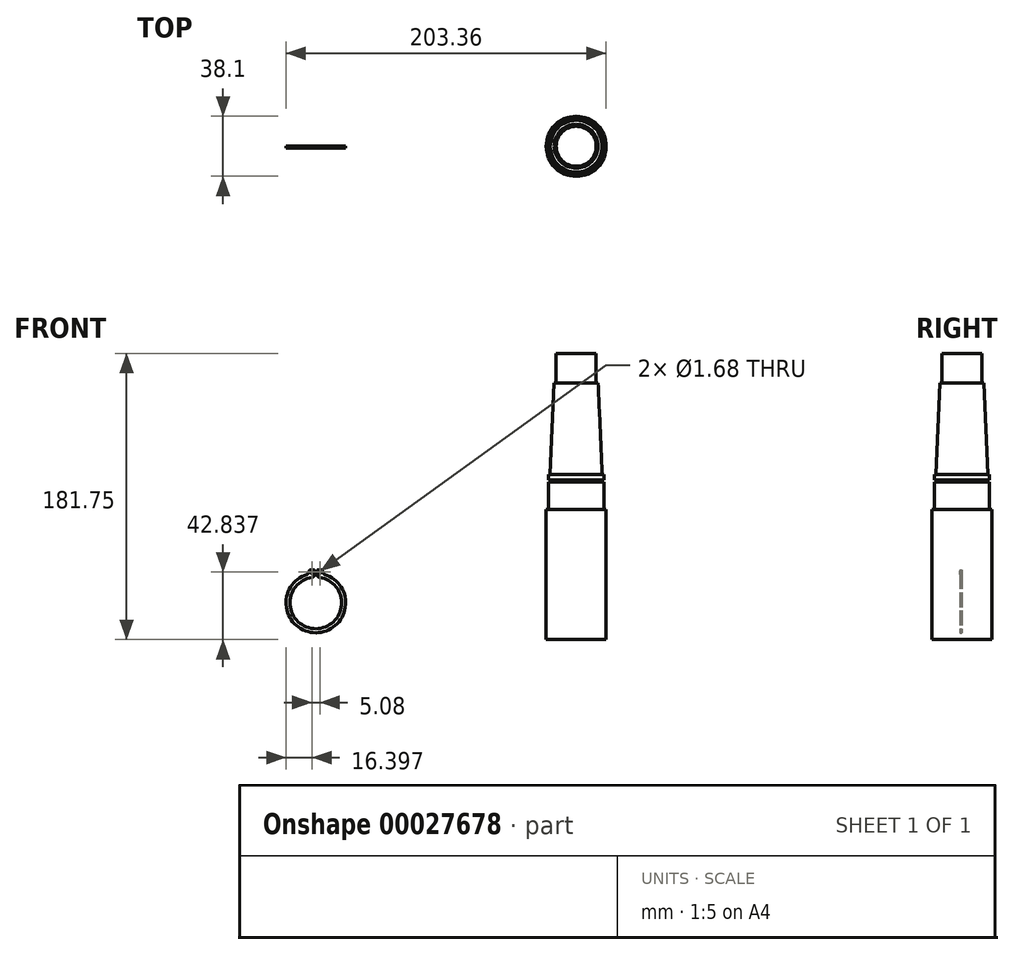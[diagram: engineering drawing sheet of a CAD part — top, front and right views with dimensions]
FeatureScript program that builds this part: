
annotation { "Feature Type Name" : "Feature", "Feature Type Description" : "" }
export const myFeature = defineFeature(function(context is Context, id is Id, definition is map)
    precondition{}
    {
        {
            var Q0;
            Q0=qCreatedBy(makeId("Top.planeOp"),FACE);
            var sketch = newSketch(context, id + "F0", { "sketchPlane" : qUnion([Q0])});
            skCircle(sketch, "E0", {"center": v(0, 0) * mm, "radius": 19.05 * mm});
            skSolve(sketch);
        }
        {
            var Q0;
            Q0 = qSketchRegion(id + "F0", true);
            extrude(context, id + "F1", {"entities" : qUnion([Q0]), "depth" : 82.75 * mm});
        }
        {
            var Q0;
            Q0=makeQuery(id+"F1.opExtrude","CAP_FACE",FACE,{"disambiguationData":[OSD([sQuery(id+"F0.wireOp",EDGE,"E0")])],"isStart":false});
            var sketch = newSketch(context, id + "F2", { "sketchPlane" : qUnion([Q0])});
            skCircle(sketch, "E1", {"center": v(0, 0) * mm, "radius": 17.5 * mm});
            skSolve(sketch);
        }
        {
            var Q0;
            Q0 = qSketchRegion(id + "F2", true);
            extrude(context, id + "F3", {"entities" : qUnion([Q0]), "operationType" : NewBodyOperationType.ADD, "depth" : 22 * mm});
        }
        {
            var Q0;
            Q0=makeQuery(id+"F3.opExtrude","CAP_FACE",FACE,{"disambiguationData":[OSD([sQuery(id+"F2.wireOp",EDGE,"E1")])],"isStart":false});
            var sketch = newSketch(context, id + "F4", { "sketchPlane" : qUnion([Q0])});
            skCircle(sketch, "E2", {"center": v(0, 0) * mm, "radius": 16.5 * mm});
            skSolve(sketch);
        }
        {
            var Q0;
            Q0 = qSketchRegion(id + "F4", true);
            extrude(context, id + "F5", {"entities" : qUnion([Q0]), "operationType" : NewBodyOperationType.ADD, "depth" : 101.6 * mm - 25.4 * mm - 18 * mm, "hasDraft" : true, "draftAngle" : 2.5 * degree, "draftPullDirection" : true});
        }
        {
            var Q0;
            Q0=makeQuery(id+"F5.opExtrude","CAP_FACE",FACE,{"disambiguationData":[OSD([sQuery(id+"F4.wireOp",EDGE,"E2")])],"isStart":false});
            var sketch = newSketch(context, id + "F6", { "sketchPlane" : qUnion([Q0])});
            skCircle(sketch, "E3", {"center": v(0, 0) * mm, "radius": 12.7 * mm});
            skSolve(sketch);
        }
        {
            var Q0;
            Q0 = qSketchRegion(id + "F6", true);
            extrude(context, id + "F7", {"entities" : qUnion([Q0]), "operationType" : NewBodyOperationType.ADD, "depth" : 18.8 * mm});
        }
        {
            var Q0;
            Q0=qCreatedBy(makeId("Front.planeOp"),FACE);
            var sketch = newSketch(context, id + "F8", { "sketchPlane" : qUnion([Q0])});
            skLineSegment(sketch, "E4.bottom", {"start": v(-18.98, 101.38) * mm, "end": v(-16.4, 101.38) * mm});
            skLineSegment(sketch, "E4.top", {"start": v(-18.98, 99.95) * mm, "end": v(-16.4, 99.95) * mm});
            skLineSegment(sketch, "E4.left", {"start": v(-18.98, 101.38) * mm, "end": v(-18.98, 99.95) * mm});
            skLineSegment(sketch, "E4.right", {"start": v(-16.4, 101.38) * mm, "end": v(-16.4, 99.95) * mm});
            skLineSegment(sketch, "E5", {"start": v(0, 106.8) * mm, "end": v(0, 83.87) * mm, "construction": true});
            skSolve(sketch);
        }
        {
            var Q0;
            Q0=makeQuery(id+"F8.imprint","IMPRINT",FACE,{"disambiguationData":[TD([[makeQuery(id+"F8.imprint","IMPRINT",EDGE,{"derivedFrom":sQuery(id+"F8.wireOp",EDGE,"E4.bottom")}),-1.0]])]});
            var Q1;
            Q1=sQuery(id+"F8.wireOp",EDGE,"E5");
            revolve(context, id + "F9", {"operationType" : NewBodyOperationType.REMOVE, "entities" : qUnion([Q0]), "axis" : qUnion([Q1]), "revolveType" : RevolveType.FULL, "oppositeDirection" : true});
        }
        {
            var Q0;
            Q0=qCreatedBy(makeId("Front.planeOp"),FACE);
            var sketch = newSketch(context, id + "F10", { "sketchPlane" : qUnion([Q0])});
            skArc(sketch, "E6", {"start": v(-166, 39.66) * mm, "mid": v(-165.37, 6.88) * mm, "end": v(-164.74, 39.66) * mm});
            skArc(sketch, "E7", {"start": v(-169.56, 41.74) * mm, "mid": v(-165.37, 4.34) * mm, "end": v(-161.18, 41.74) * mm});
            skLineSegment(sketch, "E8", {"start": v(-165.37, 23.28) * mm, "end": v(-165.37, 48.77) * mm, "construction": true});
            skCircle(sketch, "E9", {"center": v(-167.91, 42.84) * mm, "radius": 0.84 * mm});
            skLineSegment(sketch, "E10", {"start": v(-166, 44.23) * mm, "end": v(-166, 39.66) * mm});
            skLineSegment(sketch, "E11", {"start": v(-166, 44.23) * mm, "end": v(-169.56, 44.23) * mm});
            skLineSegment(sketch, "E12", {"start": v(-169.56, 44.23) * mm, "end": v(-169.56, 41.74) * mm});
            skLineSegment(sketch, "E13.MirrorCS", {"start": v(-164.74, 44.23) * mm, "end": v(-164.74, 39.66) * mm});
            skCircle(sketch, "E14.MirrorC", {"center": v(-162.83, 42.84) * mm, "radius": 0.84 * mm});
            skLineSegment(sketch, "E15.MirrorCS", {"start": v(-164.74, 44.23) * mm, "end": v(-161.18, 44.23) * mm});
            skLineSegment(sketch, "E16.MirrorCS", {"start": v(-161.18, 44.23) * mm, "end": v(-161.18, 41.74) * mm});
            skSolve(sketch);
        }
        {
            var Q0;
            Q0 = qSketchRegion(id + "F10", true);
            extrude(context, id + "F11", {"entities" : qUnion([Q0]), "depth" : 1.27 * mm});
        }
        {
            var Q0;
            Q0=makeQuery(id+"F11.opExtrude","SWEPT_EDGE",EDGE,{"disambiguationData":[OSD([sQuery(id+"F10.wireOp",EDGE,"E6"),sQuery(id+"F10.wireOp",EDGE,"E10")])]});
            var Q1;
            Q1=makeQuery(id+"F11.opExtrude","SWEPT_EDGE",EDGE,{"disambiguationData":[OSD([sQuery(id+"F10.wireOp",EDGE,"E6"),sQuery(id+"F10.wireOp",EDGE,"E13.MirrorCS")])]});
            var Q2;
            Q2=makeQuery(id+"F11.opExtrude","SWEPT_EDGE",EDGE,{"disambiguationData":[OSD([sQuery(id+"F10.wireOp",EDGE,"E7"),sQuery(id+"F10.wireOp",EDGE,"E12")])]});
            var Q3;
            Q3=makeQuery(id+"F11.opExtrude","SWEPT_EDGE",EDGE,{"disambiguationData":[OSD([sQuery(id+"F10.wireOp",EDGE,"E7"),sQuery(id+"F10.wireOp",EDGE,"E16.MirrorCS")])]});
            fillet(context, id + "F12", {"entities" : qUnion([Q0, Q1, Q2, Q3]), "radius" : 2.03 * mm, "tangentPropagation" : true, "allowEdgeOverflow" : false});
        }
        {
            var Q0;
            Q0=makeQuery(id+"F11.opExtrude","SWEPT_EDGE",EDGE,{"disambiguationData":[OSD([sQuery(id+"F10.wireOp",EDGE,"E10"),sQuery(id+"F10.wireOp",EDGE,"E11")])]});
            var Q1;
            Q1=makeQuery(id+"F11.opExtrude","SWEPT_EDGE",EDGE,{"disambiguationData":[OSD([sQuery(id+"F10.wireOp",EDGE,"E13.MirrorCS"),sQuery(id+"F10.wireOp",EDGE,"E15.MirrorCS")])]});
            var Q2;
            Q2=makeQuery(id+"F11.opExtrude","SWEPT_EDGE",EDGE,{"disambiguationData":[OSD([sQuery(id+"F10.wireOp",EDGE,"E15.MirrorCS"),sQuery(id+"F10.wireOp",EDGE,"E16.MirrorCS")])]});
            var Q3;
            Q3=makeQuery(id+"F11.opExtrude","SWEPT_EDGE",EDGE,{"disambiguationData":[OSD([sQuery(id+"F10.wireOp",EDGE,"E11"),sQuery(id+"F10.wireOp",EDGE,"E12")])]});
            fillet(context, id + "F13", {"entities" : qUnion([Q0, Q1, Q2, Q3]), "radius" : 0.76 * mm, "tangentPropagation" : true, "allowEdgeOverflow" : false});
        }
    });
